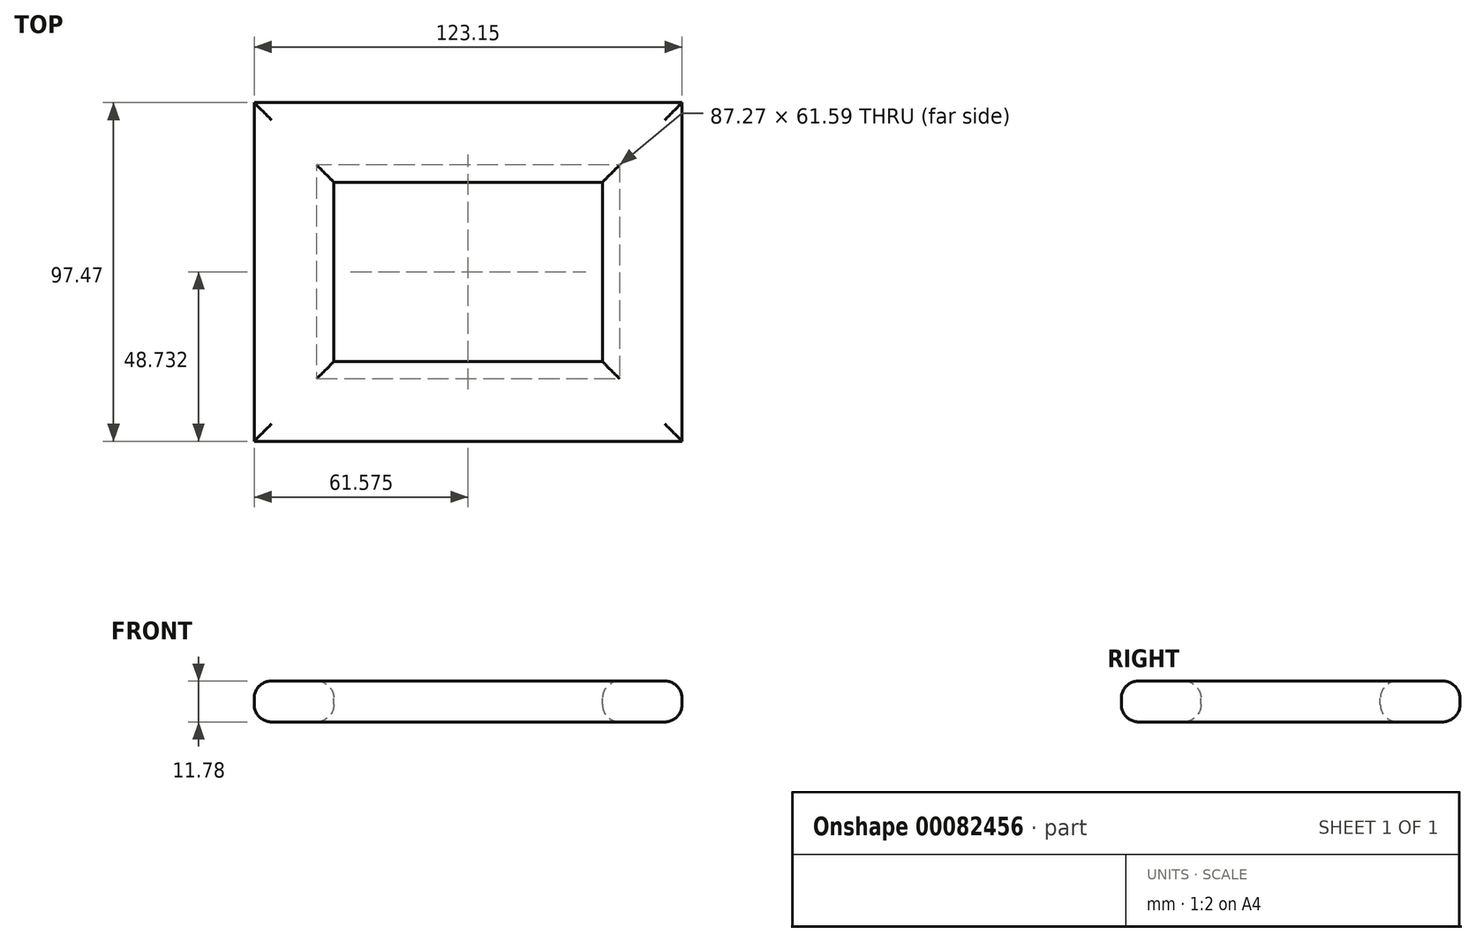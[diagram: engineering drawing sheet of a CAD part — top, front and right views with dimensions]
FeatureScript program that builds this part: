
annotation { "Feature Type Name" : "Feature", "Feature Type Description" : "" }
export const myFeature = defineFeature(function(context is Context, id is Id, definition is map)
    precondition{}
    {
        {
            var Q0;
            Q0=qCreatedBy(makeId("Top.planeOp"),FACE);
            var sketch = newSketch(context, id + "F0", { "sketchPlane" : qUnion([Q0])});
            skLineSegment(sketch, "E0.bottom", {"start": v(-49, -31.96) * mm, "end": v(46.5, -31.96) * mm});
            skLineSegment(sketch, "E0.top", {"start": v(-49, 37.86) * mm, "end": v(46.5, 37.86) * mm});
            skLineSegment(sketch, "E0.left", {"start": v(-49, -31.96) * mm, "end": v(-49, 37.86) * mm});
            skLineSegment(sketch, "E0.right", {"start": v(46.5, -31.96) * mm, "end": v(46.5, 37.86) * mm});
            skSolve(sketch);
        }
        {
            var Q0;
            Q0=sQuery(id+"F0.wireOp",VERTEX,"E0.bottom.start");
            var Q1;
            Q1=sQuery(id+"F0.wireOp",EDGE,"E0.left");
            cPlane(context, id + "F1", {"entities" : qUnion([Q0, Q1]), "cplaneType" : CPlaneType.CURVE_POINT, "offset" : 25 * mm, "width" : 150 * mm, "height" : 150 * mm});
        }
        {
            var Q0;
            Q0=qCreatedBy(id+"F1.planeOp",FACE);
            var sketch = newSketch(context, id + "F2", { "sketchPlane" : qUnion([Q0])});
            skLineSegment(sketch, "E1.bottom", {"start": v(57.82, 6.05) * mm, "end": v(44.88, 6.05) * mm});
            skLineSegment(sketch, "E1.top", {"start": v(57.82, -5.73) * mm, "end": v(44.88, -5.73) * mm});
            skLineSegment(sketch, "E1.left", {"start": v(62.82, 1.05) * mm, "end": v(62.82, -0.73) * mm});
            skLineSegment(sketch, "E1.right", {"start": v(39.88, 1.05) * mm, "end": v(39.88, -0.73) * mm});
            skPoint(sketch, "E2.visualSharp", {"position": v(62.82, 6.05) * mm});
            skArc(sketch, "E2.filletArc", {"start": v(62.82, 1.05) * mm, "mid": v(61.36, 4.58) * mm, "end": v(57.82, 6.05) * mm});
            skPoint(sketch, "E3.visualSharp", {"position": v(39.88, 6.05) * mm});
            skArc(sketch, "E3.filletArc", {"start": v(44.88, 6.05) * mm, "mid": v(41.34, 4.58) * mm, "end": v(39.88, 1.05) * mm});
            skPoint(sketch, "E4.visualSharp", {"position": v(39.88, -5.73) * mm});
            skArc(sketch, "E4.filletArc", {"start": v(39.88, -0.73) * mm, "mid": v(41.34, -4.27) * mm, "end": v(44.88, -5.73) * mm});
            skPoint(sketch, "E5.visualSharp", {"position": v(62.82, -5.73) * mm});
            skArc(sketch, "E5.filletArc", {"start": v(57.82, -5.73) * mm, "mid": v(61.36, -4.27) * mm, "end": v(62.82, -0.73) * mm});
            skSolve(sketch);
        }
        {
            var Q0;
            Q0=makeQuery(id+"F2.imprint","IMPRINT",FACE,{"disambiguationData":[TD([[makeQuery(id+"F2.imprint","IMPRINT",EDGE,{"derivedFrom":sQuery(id+"F2.wireOp",EDGE,"E1.bottom")}),1.0]])]});
            var Q1;
            Q1=sQuery(id+"F0.wireOp",EDGE,"E0.left");
            var Q2;
            Q2=sQuery(id+"F0.wireOp",EDGE,"E0.top");
            var Q3;
            Q3=sQuery(id+"F0.wireOp",EDGE,"E0.right");
            var Q4;
            Q4=sQuery(id+"F0.wireOp",EDGE,"E0.bottom");
            sweep(context, id + "F3", {"profiles" : qUnion([Q0]), "path" : qUnion([Q1, Q2, Q3, Q4])});
        }
    });
